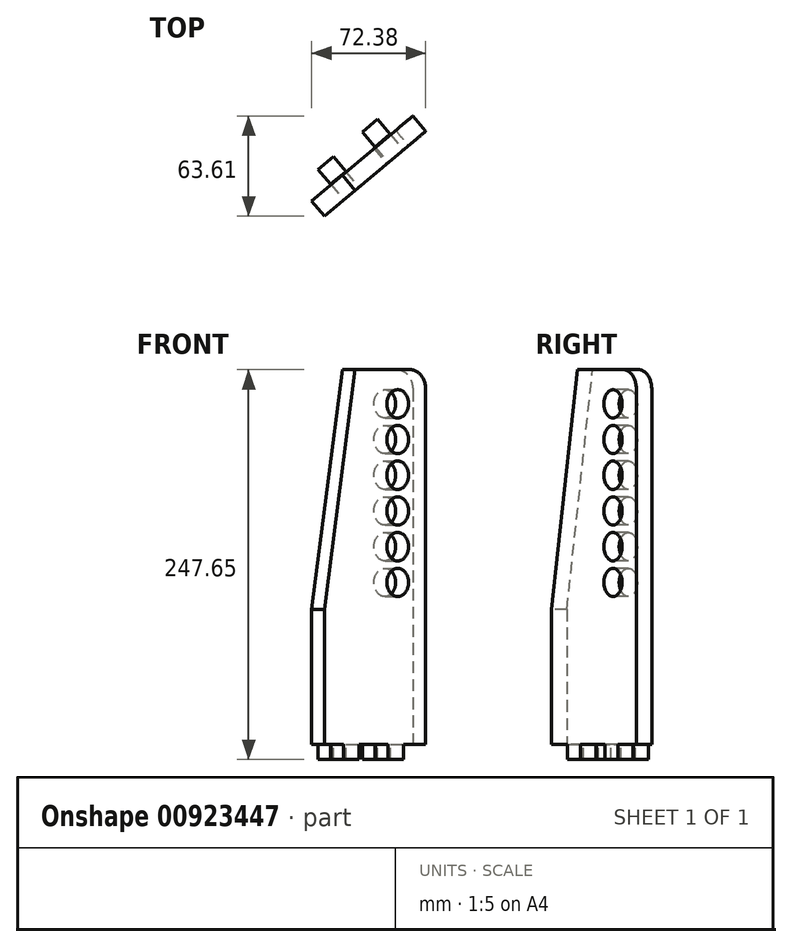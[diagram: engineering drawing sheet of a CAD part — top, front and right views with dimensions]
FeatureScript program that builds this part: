
annotation { "Feature Type Name" : "Feature", "Feature Type Description" : "" }
export const myFeature = defineFeature(function(context is Context, id is Id, definition is map)
    precondition{}
    {
        {
            var Q0;
            Q0=qCreatedBy(makeId("Top.planeOp"),FACE);
            var sketch = newSketch(context, id + "F0", { "sketchPlane" : qUnion([Q0])});
            skLineSegment(sketch, "E0", {"start": v(-180.97, -66.34) * mm, "end": v(180.97, -66.34) * mm, "construction": true});
            skLineSegment(sketch, "E1", {"start": v(-180.98, 35.26) * mm, "end": v(180.98, 35.26) * mm, "construction": true});
            skLineSegment(sketch, "E2", {"start": v(-164.22, -44.12) * mm, "end": v(164.22, -44.12) * mm, "construction": true});
            skPoint(sketch, "E3", {"position": v(0, 35.26) * mm});
            skPoint(sketch, "E4", {"position": v(0, -44.12) * mm});
            skPoint(sketch, "E5", {"position": v(0, -66.34) * mm});
            skLineSegment(sketch, "E6", {"start": v(-180.97, 35.26) * mm, "end": v(-180.97, -66.34) * mm, "construction": true});
            skLineSegment(sketch, "E7", {"start": v(180.98, 35.26) * mm, "end": v(180.98, -66.34) * mm, "construction": true});
            skLineSegment(sketch, "E8", {"start": v(-180.97, 9.86) * mm, "end": v(180.97, 9.86) * mm, "construction": true});
            skArc(sketch, "E9", {"start": v(180.97, 9.86) * mm, "mid": v(0, 35.26) * mm, "end": v(-180.97, 9.86) * mm});
            skArc(sketch, "E10.0", {"start": v(159.12, -66.45) * mm, "mid": v(0, -44.12) * mm, "end": v(-159.12, -66.45) * mm});
            skLineSegment(sketch, "E11", {"start": v(-180.97, 9.86) * mm, "end": v(-159.12, -66.45) * mm});
            skLineSegment(sketch, "E12", {"start": v(180.97, 9.86) * mm, "end": v(159.12, -66.45) * mm});
            skArc(sketch, "E13.0", {"start": v(164.71, -38.5) * mm, "mid": v(0, -15.7) * mm, "end": v(-164.71, -38.5) * mm, "construction": true});
            skPoint(sketch, "E14.center", {"position": v(0, 0) * mm});
            skPoint(sketch, "E15", {"position": v(139.85, -32.05) * mm});
            skPoint(sketch, "E16", {"position": v(80.31, -21.05) * mm});
            skArc(sketch, "E17.0.startCap", {"start": v(36.04, -107.67) * mm, "mid": v(26.04, -97.67) * mm, "end": v(36.04, -87.67) * mm});
            skArc(sketch, "E17.0.endCap", {"start": v(56.04, -87.67) * mm, "mid": v(66.04, -97.67) * mm, "end": v(56.04, -107.67) * mm});
            skLineSegment(sketch, "E17.0.left", {"start": v(36.04, -87.67) * mm, "end": v(56.04, -87.67) * mm});
            skLineSegment(sketch, "E17.0.right", {"start": v(36.04, -107.67) * mm, "end": v(56.04, -107.67) * mm});
            skPoint(sketch, "E18", {"position": v(-97.74, -23.63) * mm});
            skPoint(sketch, "E19", {"position": v(-51.33, -17.88) * mm});
            skArc(sketch, "E20.0.startCap", {"start": v(118.42, -38.42) * mm, "mid": v(110.3, -26.84) * mm, "end": v(121.9, -18.73) * mm});
            skArc(sketch, "E20.0.endCap", {"start": v(141.59, -22.2) * mm, "mid": v(149.7, -33.79) * mm, "end": v(138.11, -41.9) * mm});
            skLineSegment(sketch, "E20.0.left", {"start": v(121.9, -18.73) * mm, "end": v(141.59, -22.2) * mm});
            skLineSegment(sketch, "E20.0.right", {"start": v(118.42, -38.42) * mm, "end": v(138.11, -41.9) * mm});
            skArc(sketch, "E21.0.startCap", {"start": v(59.52, -29.26) * mm, "mid": v(50.43, -18.43) * mm, "end": v(61.26, -9.34) * mm});
            skArc(sketch, "E21.0.endCap", {"start": v(81.19, -11.08) * mm, "mid": v(90.28, -21.92) * mm, "end": v(79.44, -31) * mm});
            skLineSegment(sketch, "E21.0.left", {"start": v(61.26, -9.34) * mm, "end": v(81.19, -11.08) * mm});
            skLineSegment(sketch, "E21.0.right", {"start": v(59.52, -29.26) * mm, "end": v(79.44, -31) * mm});
            skArc(sketch, "E22.0.startCap", {"start": v(-96, -33.48) * mm, "mid": v(-107.59, -25.37) * mm, "end": v(-99.48, -13.78) * mm});
            skArc(sketch, "E22.0.endCap", {"start": v(-79.78, -10.31) * mm, "mid": v(-68.2, -18.42) * mm, "end": v(-76.3, -30) * mm});
            skLineSegment(sketch, "E22.0.left", {"start": v(-99.48, -13.78) * mm, "end": v(-79.78, -10.31) * mm});
            skLineSegment(sketch, "E22.0.right", {"start": v(-96, -33.48) * mm, "end": v(-76.3, -30) * mm});
            skArc(sketch, "E23.0.startCap", {"start": v(-50.46, -27.84) * mm, "mid": v(-61.3, -18.75) * mm, "end": v(-52.2, -7.92) * mm});
            skArc(sketch, "E23.0.endCap", {"start": v(-32.28, -6.18) * mm, "mid": v(-21.45, -15.27) * mm, "end": v(-30.54, -26.1) * mm});
            skLineSegment(sketch, "E23.0.left", {"start": v(-52.2, -7.92) * mm, "end": v(-32.28, -6.18) * mm});
            skLineSegment(sketch, "E23.0.right", {"start": v(-50.46, -27.84) * mm, "end": v(-30.54, -26.1) * mm});
            skLineSegment(sketch, "E24.bottom", {"start": v(-12.69, -27.76) * mm, "end": v(51.52, 26.12) * mm});
            skLineSegment(sketch, "E24.top", {"start": v(-4.52, -37.49) * mm, "end": v(59.69, 16.4) * mm});
            skLineSegment(sketch, "E24.left", {"start": v(-12.69, -27.76) * mm, "end": v(-4.52, -37.49) * mm});
            skLineSegment(sketch, "E24.right", {"start": v(51.52, 26.12) * mm, "end": v(59.69, 16.4) * mm});
            skLineSegment(sketch, "E25.0", {"start": v(-21.63, -26.98) * mm, "end": v(-5.3, -46.43) * mm, "construction": true});
            skLineSegment(sketch, "E25.1", {"start": v(-21.63, -26.98) * mm, "end": v(52.3, 35.07) * mm, "construction": true});
            skLineSegment(sketch, "E25.2", {"start": v(52.3, 35.07) * mm, "end": v(68.63, 15.6) * mm, "construction": true});
            skLineSegment(sketch, "E25.3", {"start": v(-5.3, -46.43) * mm, "end": v(68.63, 15.6) * mm, "construction": true});
            skPoint(sketch, "E26.visualSharp", {"position": v(-21.63, -26.98) * mm});
            skPoint(sketch, "E27.visualSharp", {"position": v(-5.3, -46.43) * mm});
            skPoint(sketch, "E28.visualSharp", {"position": v(68.63, 15.6) * mm});
            skPoint(sketch, "E29.visualSharp", {"position": v(52.3, 35.07) * mm});
            skLineSegment(sketch, "E30", {"start": v(9.2, -9.4) * mm, "end": v(17.37, -19.12) * mm});
            skLineSegment(sketch, "E31", {"start": v(-0.53, -17.55) * mm, "end": v(7.64, -27.28) * mm});
            skLineSegment(sketch, "E32", {"start": v(27.69, 6.12) * mm, "end": v(35.85, -3.6) * mm});
            skLineSegment(sketch, "E33", {"start": v(37.42, 14.28) * mm, "end": v(45.58, 4.56) * mm});
            skLineSegment(sketch, "E34", {"start": v(27.69, 6.12) * mm, "end": v(37.42, 14.28) * mm});
            skLineSegment(sketch, "E35", {"start": v(45.58, 4.56) * mm, "end": v(35.85, -3.6) * mm});
            skLineSegment(sketch, "E36", {"start": v(17.37, -19.12) * mm, "end": v(7.64, -27.28) * mm});
            skLineSegment(sketch, "E37", {"start": v(-0.53, -17.55) * mm, "end": v(9.2, -9.4) * mm});
            skLineSegment(sketch, "E38.0", {"start": v(-1.06, -17.5) * mm, "end": v(9.25, -8.85) * mm});
            skLineSegment(sketch, "E38.2", {"start": v(7.6, -27.82) * mm, "end": v(17.9, -19.17) * mm});
            skLineSegment(sketch, "E39.0", {"start": v(37.46, 14.82) * mm, "end": v(46.12, 4.5) * mm});
            skLineSegment(sketch, "E40.0", {"start": v(27.15, 6.17) * mm, "end": v(35.8, -4.15) * mm});
            skLineSegment(sketch, "E41.0", {"start": v(9.25, -8.85) * mm, "end": v(17.9, -19.17) * mm});
            skLineSegment(sketch, "E42.0", {"start": v(-1.06, -17.5) * mm, "end": v(7.6, -27.82) * mm});
            skLineSegment(sketch, "E43.trimOffspring", {"start": v(35.8, -4.15) * mm, "end": v(46.12, 4.5) * mm});
            skLineSegment(sketch, "E44.trimOffspring", {"start": v(27.15, 6.17) * mm, "end": v(37.46, 14.82) * mm});
            skPoint(sketch, "E45.visualSharp", {"position": v(-180.98, 9.86) * mm});
            skPoint(sketch, "E46.visualSharp", {"position": v(-159.12, -66.45) * mm});
            skPoint(sketch, "E47.visualSharp", {"position": v(159.12, -66.45) * mm});
            skPoint(sketch, "E48.visualSharp", {"position": v(180.97, 9.86) * mm});
            skSolve(sketch);
        }
        {
            var Q0;
            Q0=makeQuery(id+"F0.imprint","IMPRINT",FACE,{"disambiguationData":[TD([[makeQuery(id+"F0.imprint","IMPRINT",EDGE,{"derivedFrom":sQuery(id+"F0.wireOp",EDGE,"E9")}),1.0]])]});
            var Q1;
            {var subQ0=sQuery(id+"F0.wireOp",EDGE,"E24.left");Q1=makeQuery(id+"F0.imprint","IMPRINT",FACE,{"disambiguationData":[TD([[makeQuery(id+"F0.imprint","IMPRINT",EDGE,{"derivedFrom":subQ0}),1.0]])]});}
            var Q2;
            {var subQ0=sQuery(id+"F0.wireOp",EDGE,"E41.0");var subQ1=sQuery(id+"F0.wireOp",EDGE,"E24.bottom");var subQ2=makeQuery(id+"F0.imprint","INTERSECT",VERTEX,{"derivedFrom":[subQ1,subQ0]});Q2=makeQuery(id+"F0.imprint","IMPRINT",FACE,{"disambiguationData":[TD([[makeQuery(id+"F0.imprint","IMPRINT",EDGE,{"disambiguationData":[TD([[subQ2,-1.0]])],"derivedFrom":subQ1}),-1.0]])]});}
            var Q3;
            {var subQ0=sQuery(id+"F0.wireOp",EDGE,"E24.right");Q3=makeQuery(id+"F0.imprint","IMPRINT",FACE,{"disambiguationData":[TD([[makeQuery(id+"F0.imprint","IMPRINT",EDGE,{"derivedFrom":subQ0}),-1.0]])]});}
            extrude(context, id + "F1", {"entities" : qUnion([Q0, Q1, Q2, Q3]), "oppositeDirection" : true, "depth" : 12.7 * mm, "offsetDistance" : 25.4 * mm});
        }
        {
            var Q0;
            Q0=makeQuery(id+"F0.imprint","IMPRINT",FACE,{"disambiguationData":[TD([[makeQuery(id+"F0.imprint","IMPRINT",EDGE,{"derivedFrom":sQuery(id+"F0.wireOp",EDGE,"E24.bottom")}),-1.0]])]});
            extrude(context, id + "F2", {"entities" : qUnion([Q0]), "depth" : 238.12 * mm, "offsetDistance" : 25.4 * mm});
        }
        {
            var Q0;
            {var subQ2=sQuery(id+"F0.wireOp",EDGE,"E30");Q0=makeQuery(id+"F0.imprint","IMPRINT",FACE,{"disambiguationData":[TD([[makeQuery(id+"F0.imprint","IMPRINT",EDGE,{"derivedFrom":subQ2}),-1.0]])]});}
            var Q1;
            {var subQ0=sQuery(id+"F0.wireOp",EDGE,"E32");Q1=makeQuery(id+"F0.imprint","IMPRINT",FACE,{"disambiguationData":[TD([[makeQuery(id+"F0.imprint","IMPRINT",EDGE,{"derivedFrom":subQ0}),1.0]])]});}
            extrude(context, id + "F3", {"entities" : qUnion([Q0, Q1]), "operationType" : NewBodyOperationType.ADD, "oppositeDirection" : true, "depth" : 9.52 * mm, "offsetDistance" : 25.4 * mm});
        }
        {
            var Q0;
            {var subQ0=sQuery(id+"F0.wireOp",EDGE,"E24.top");Q0=makeQuery(id+"F3.boolean.opBoolean","MERGE",FACE,{"derivedFrom":[makeQuery(id+"F2.opExtrude","SWEPT_FACE",FACE,{"disambiguationData":[OSD([subQ0])]}),makeQuery(id+"F3.opExtrude","SWEPT_FACE",FACE,{"disambiguationData":[OSD([subQ0]),TDD([makeQuery(id+"F0.imprint","IMPRINT",EDGE,{"disambiguationData":[TD([[makeQuery(id+"F0.imprint","INTERSECT",VERTEX,{"derivedFrom":[subQ0,sQuery(id+"F0.wireOp",EDGE,"E32")]}),-1.0]])],"derivedFrom":subQ0})])]}),makeQuery(id+"F3.opExtrude","SWEPT_FACE",FACE,{"disambiguationData":[OSD([subQ0]),TDD([makeQuery(id+"F0.imprint","IMPRINT",EDGE,{"disambiguationData":[TD([[makeQuery(id+"F0.imprint","INTERSECT",VERTEX,{"derivedFrom":[subQ0,sQuery(id+"F0.wireOp",EDGE,"E31")]}),-1.0]])],"derivedFrom":subQ0})])]})]});}
            var sketch = newSketch(context, id + "F4", { "sketchPlane" : qUnion([Q0])});
            skCircle(sketch, "E49", {"center": v(33.06, 216.43) * mm, "radius": 9 * mm});
            skCircle(sketch, "E50.0.1.0", {"center": v(33.06, 193.74) * mm, "radius": 9 * mm});
            skCircle(sketch, "E50.0.2.0", {"center": v(33.06, 171.05) * mm, "radius": 9 * mm});
            skCircle(sketch, "E50.0.3.0", {"center": v(33.06, 148.36) * mm, "radius": 9 * mm});
            skCircle(sketch, "E50.0.4.0", {"center": v(33.06, 125.67) * mm, "radius": 9 * mm});
            skCircle(sketch, "E50.0.5.0", {"center": v(33.06, 102.98) * mm, "radius": 9 * mm});
            skLineSegment(sketch, "E50.direction1", {"start": v(33.06, 216.43) * mm, "end": v(58.46, 216.43) * mm, "construction": true});
            skLineSegment(sketch, "E50.direction2", {"start": v(33.06, 216.43) * mm, "end": v(33.06, 193.74) * mm, "construction": true});
            skPoint(sketch, "E51", {"position": v(-2.16, 238.13) * mm});
            skPoint(sketch, "E52", {"position": v(-27.56, 85.72) * mm});
            skLineSegment(sketch, "E53", {"start": v(-2.16, 238.13) * mm, "end": v(-27.56, 85.72) * mm});
            skLineSegment(sketch, "E54", {"start": v(-2.16, 238.13) * mm, "end": v(56.26, 238.13) * mm});
            skLineSegment(sketch, "E55", {"start": v(56.26, 238.13) * mm, "end": v(56.26, 0) * mm});
            skLineSegment(sketch, "E56", {"start": v(56.26, 0) * mm, "end": v(37.84, 0) * mm});
            skLineSegment(sketch, "E57", {"start": v(37.84, 0) * mm, "end": v(37.84, -9.53) * mm});
            skLineSegment(sketch, "E58", {"start": v(37.84, -9.53) * mm, "end": v(25.14, -9.53) * mm});
            skLineSegment(sketch, "E59", {"start": v(25.14, -9.53) * mm, "end": v(25.14, 0) * mm});
            skLineSegment(sketch, "E60", {"start": v(25.14, 0) * mm, "end": v(1.01, 0) * mm});
            skLineSegment(sketch, "E61", {"start": v(1.01, 0) * mm, "end": v(1.01, -9.53) * mm});
            skLineSegment(sketch, "E62", {"start": v(1.01, -9.53) * mm, "end": v(-11.69, -9.53) * mm});
            skLineSegment(sketch, "E63", {"start": v(-11.69, -9.53) * mm, "end": v(-11.69, 0) * mm});
            skLineSegment(sketch, "E64", {"start": v(-11.69, 0) * mm, "end": v(-27.56, 0) * mm});
            skLineSegment(sketch, "E65", {"start": v(-27.56, 0) * mm, "end": v(-27.56, 85.73) * mm});
            skPoint(sketch, "E66.visualSharp", {"position": v(56.26, 238.13) * mm});
            skSolve(sketch);
        }
        {
            var Q0;
            Q0=makeQuery(id+"F4.imprint","IMPRINT",FACE,{"disambiguationData":[TD([[makeQuery(id+"F4.imprint","IMPRINT",EDGE,{"derivedFrom":sQuery(id+"F4.wireOp",EDGE,"E49")}),-1.0]])]});
            extrude(context, id + "F5", {"entities" : qUnion([Q0]), "operationType" : NewBodyOperationType.INTERSECT, "oppositeDirection" : true, "depth" : 25.4 * mm, "offsetDistance" : 25.4 * mm});
        }
        {
            var Q0;
            Q0=makeQuery(id+"F5.boolean.opBoolean","COPY",EDGE,{"derivedFrom":makeQuery(id+"F5.boolean.toolComplement.opBoolean","COPY",EDGE,{"derivedFrom":makeQuery(id+"F5.opExtrude","SWEPT_EDGE",EDGE,{"disambiguationData":[OSD([sQuery(id+"F0.wireOp",EDGE,"E24.top"),sQuery(id+"F4.wireOp",EDGE,"E53"),sQuery(id+"F4.wireOp",EDGE,"E54")])]})})});
            var Q1;
            Q1=makeQuery(id+"F2.opExtrude","CAP_EDGE",EDGE,{"disambiguationData":[OSD([sQuery(id+"F0.wireOp",EDGE,"E24.right")])],"isStart":false});
            var Q2;
            Q2=makeQuery(id+"F5.boolean.opBoolean","COPY",EDGE,{"derivedFrom":makeQuery(id+"F5.boolean.toolComplement.opBoolean","COPY",EDGE,{"derivedFrom":makeQuery(id+"F5.opExtrude","SWEPT_EDGE",EDGE,{"disambiguationData":[OSD([sQuery(id+"F0.wireOp",EDGE,"E24.top"),sQuery(id+"F0.wireOp",EDGE,"E24.left"),sQuery(id+"F4.wireOp",EDGE,"E53"),sQuery(id+"F4.wireOp",EDGE,"E65")])]})})});
            var Q3;
            Q3=makeQuery(id+"F1.opExtrude","SWEPT_EDGE",EDGE,{"disambiguationData":[OSD([sQuery(id+"F0.wireOp",EDGE,"E10.0"),sQuery(id+"F0.wireOp",EDGE,"E12")])]});
            var Q4;
            Q4=makeQuery(id+"F1.opExtrude","SWEPT_EDGE",EDGE,{"disambiguationData":[OSD([sQuery(id+"F0.wireOp",EDGE,"E9"),sQuery(id+"F0.wireOp",EDGE,"E12")])]});
            var Q5;
            Q5=makeQuery(id+"F1.opExtrude","SWEPT_EDGE",EDGE,{"disambiguationData":[OSD([sQuery(id+"F0.wireOp",EDGE,"E10.0"),sQuery(id+"F0.wireOp",EDGE,"E11")])]});
            var Q6;
            Q6=makeQuery(id+"F1.opExtrude","SWEPT_EDGE",EDGE,{"disambiguationData":[OSD([sQuery(id+"F0.wireOp",EDGE,"E9"),sQuery(id+"F0.wireOp",EDGE,"E11")])]});
            fillet(context, id + "F6", {"entities" : qUnion([Q0, Q1, Q2, Q3, Q4, Q5, Q6]), "tangentPropagation" : true, "radius" : 12.7 * mm, "defaultsChanged" : true, "vertexSettings" : [], "allowEdgeOverflow" : false});
        }
    });
